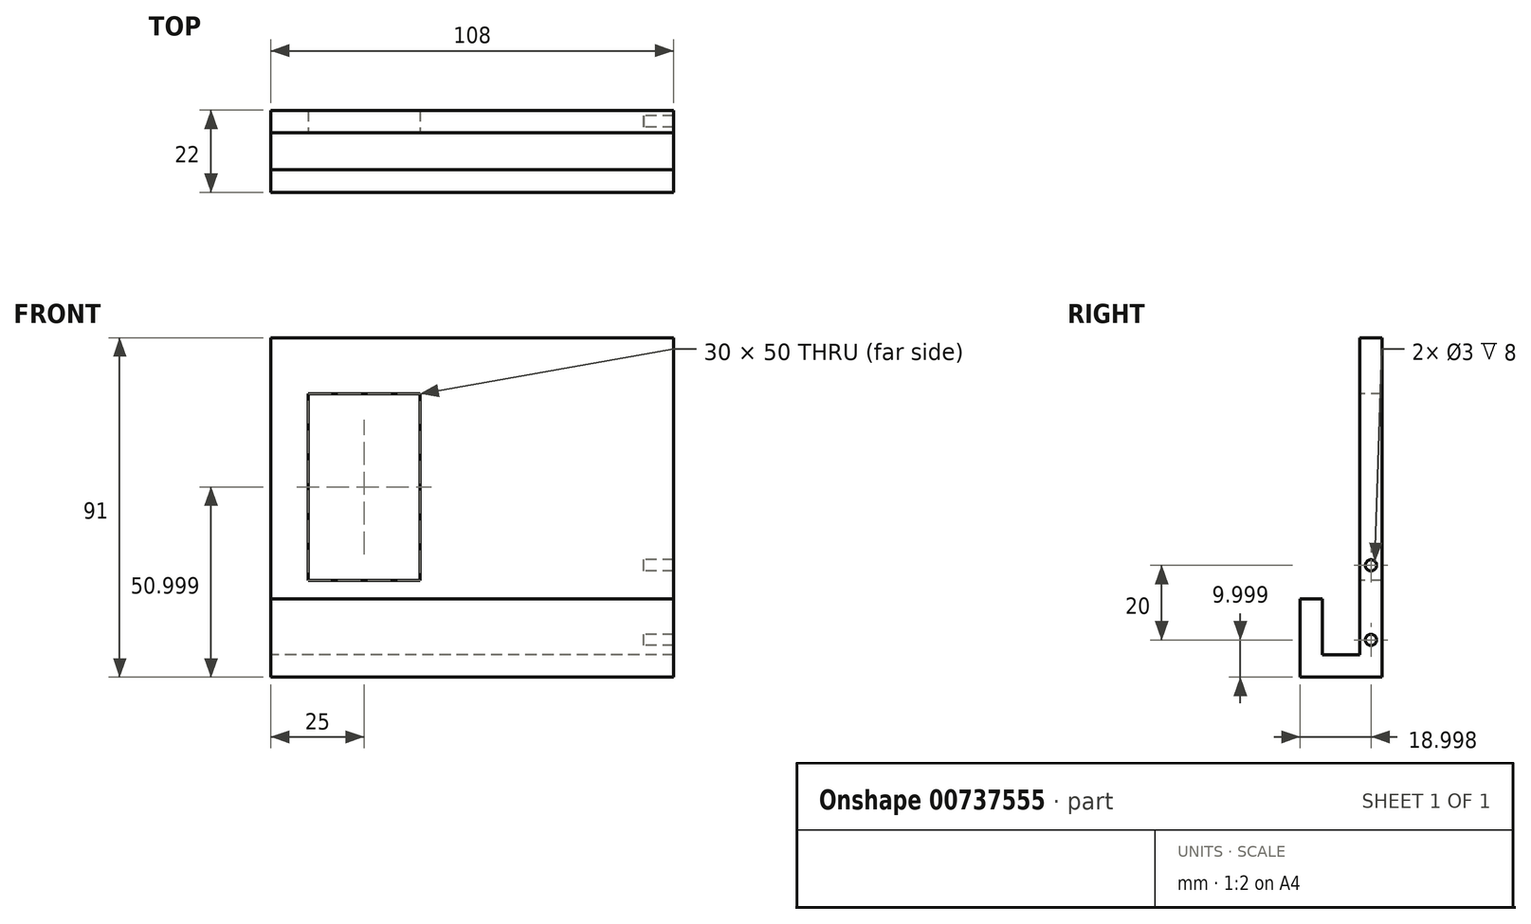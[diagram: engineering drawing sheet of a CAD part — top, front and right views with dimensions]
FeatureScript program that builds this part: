
annotation { "Feature Type Name" : "Feature", "Feature Type Description" : "" }
export const myFeature = defineFeature(function(context is Context, id is Id, definition is map)
    precondition{}
    {
        {
            var Q0;
            Q0=qCreatedBy(makeId("Right.planeOp"),FACE);
            var sketch = newSketch(context, id + "F0", { "sketchPlane" : qUnion([Q0])});
            skLineSegment(sketch, "E0", {"start": v(21.48, 53.88) * mm, "end": v(21.48, -37.12) * mm});
            skLineSegment(sketch, "E1", {"start": v(-0.52, -37.12) * mm, "end": v(21.48, -37.12) * mm});
            skLineSegment(sketch, "E2", {"start": v(-0.52, -37.12) * mm, "end": v(-0.52, -16.12) * mm});
            skLineSegment(sketch, "E3", {"start": v(5.48, -16.12) * mm, "end": v(5.48, -31.12) * mm});
            skLineSegment(sketch, "E4", {"start": v(5.48, -31.12) * mm, "end": v(15.48, -31.12) * mm});
            skLineSegment(sketch, "E5", {"start": v(15.48, -31.12) * mm, "end": v(15.48, 53.88) * mm});
            skLineSegment(sketch, "E6", {"start": v(15.48, 53.88) * mm, "end": v(21.48, 53.88) * mm});
            skLineSegment(sketch, "E7", {"start": v(-0.52, -16.12) * mm, "end": v(5.48, -16.12) * mm});
            skSolve(sketch);
        }
        {
            var Q0;
            Q0=makeQuery(id+"F0.imprint","IMPRINT",FACE,{"disambiguationData":[TD([[makeQuery(id+"F0.imprint","IMPRINT",EDGE,{"derivedFrom":sQuery(id+"F0.wireOp",EDGE,"E0")}),-1.0]])]});
            extrude(context, id + "F1", {"entities" : qUnion([Q0]), "depth" : 100 * mm, "offsetDistance" : 25 * mm});
        }
        {
            var Q0;
            Q0=makeQuery(id+"F1.opExtrude","SWEPT_FACE",FACE,{"disambiguationData":[OSD([sQuery(id+"F0.wireOp",EDGE,"E5")])]});
            var sketch = newSketch(context, id + "F2", { "sketchPlane" : qUnion([Q0])});
            skLineSegment(sketch, "E8", {"start": v(0, -31.12) * mm, "end": v(0, -11.12) * mm});
            skLineSegment(sketch, "E9", {"start": v(0, -11.12) * mm, "end": v(10, -11.12) * mm});
            skLineSegment(sketch, "E10.bottom", {"start": v(10, -11.12) * mm, "end": v(40, -11.12) * mm});
            skLineSegment(sketch, "E10.top", {"start": v(10, 38.88) * mm, "end": v(40, 38.88) * mm});
            skLineSegment(sketch, "E10.left", {"start": v(10, -11.12) * mm, "end": v(10, 38.88) * mm});
            skLineSegment(sketch, "E10.right", {"start": v(40, -11.12) * mm, "end": v(40, 38.88) * mm});
            skSolve(sketch);
        }
        {
            var Q0;
            Q0=makeQuery(id+"F2.imprint","IMPRINT",FACE,{"disambiguationData":[TD([[makeQuery(id+"F2.imprint","IMPRINT",EDGE,{"derivedFrom":sQuery(id+"F2.wireOp",EDGE,"E10.bottom")}),1.0]])]});
            extrude(context, id + "F3", {"entities" : qUnion([Q0]), "operationType" : NewBodyOperationType.REMOVE, "oppositeDirection" : true, "depth" : 6 * mm, "offsetDistance" : 25 * mm});
        }
        {
            var Q0;
            Q0=makeQuery(id+"F1.opExtrude","CAP_FACE",FACE,{"disambiguationData":[OSD([sQuery(id+"F0.wireOp",EDGE,"E0"),sQuery(id+"F0.wireOp",EDGE,"E1"),sQuery(id+"F0.wireOp",EDGE,"E2"),sQuery(id+"F0.wireOp",EDGE,"E3"),sQuery(id+"F0.wireOp",EDGE,"E4"),sQuery(id+"F0.wireOp",EDGE,"E5"),sQuery(id+"F0.wireOp",EDGE,"E6"),sQuery(id+"F0.wireOp",EDGE,"E7")])],"isStart":false});
            var sketch = newSketch(context, id + "F4", { "sketchPlane" : qUnion([Q0])});
            skCircle(sketch, "E11", {"center": v(18.48, 43.88) * mm, "radius": 1.5 * mm});
            skCircle(sketch, "E12", {"center": v(18.48, 23.88) * mm, "radius": 1.5 * mm});
            skCircle(sketch, "E13.MirrorC", {"center": v(18.48, -27.12) * mm, "radius": 1.5 * mm});
            skCircle(sketch, "E14.MirrorC", {"center": v(18.48, -7.12) * mm, "radius": 1.5 * mm});
            skSolve(sketch);
        }
        {
            var Q0;
            Q0=makeQuery(id+"F4.imprint","IMPRINT",FACE,{"disambiguationData":[TD([[makeQuery(id+"F4.imprint","IMPRINT",EDGE,{"derivedFrom":sQuery(id+"F4.wireOp",EDGE,"E11")}),1.0]])]});
            var Q1;
            Q1=makeQuery(id+"F4.imprint","IMPRINT",FACE,{"disambiguationData":[TD([[makeQuery(id+"F4.imprint","IMPRINT",EDGE,{"derivedFrom":sQuery(id+"F4.wireOp",EDGE,"E12")}),1.0]])]});
            var Q2;
            Q2=makeQuery(id+"F4.imprint","IMPRINT",FACE,{"disambiguationData":[TD([[makeQuery(id+"F4.imprint","IMPRINT",EDGE,{"derivedFrom":sQuery(id+"F4.wireOp",EDGE,"E14.MirrorC")}),-1.0]])]});
            var Q3;
            Q3=makeQuery(id+"F4.imprint","IMPRINT",FACE,{"disambiguationData":[TD([[makeQuery(id+"F4.imprint","IMPRINT",EDGE,{"derivedFrom":sQuery(id+"F4.wireOp",EDGE,"E13.MirrorC")}),-1.0]])]});
            extrude(context, id + "F5", {"entities" : qUnion([Q0, Q1, Q2, Q3]), "operationType" : NewBodyOperationType.ADD, "depth" : 8 * mm, "offsetDistance" : 25 * mm});
        }
    });
